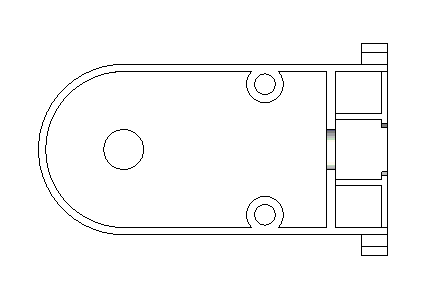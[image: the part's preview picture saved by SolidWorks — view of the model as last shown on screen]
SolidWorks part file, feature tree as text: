
SOLIDWORKS PART (.sldprt)
format: sldprt  version: not decoded by parser v0  size: 378,368 bytes
history: native  units: mm
features: sketch x12, cut_extrude x9, extrude x3, plane x1, mirror x1 (+10 scaffold rows collapsed)
feature tree (36):
  scaffold x10  (default folders/planes/origin — collapsed)
  sketch  "Sketch1"  dims[c1.D1=19.9644mm c1.D4=19.9644mm c2.D1=2.286mm c2.D2=2.9718mm c2.D3=2.413mm c2.D4=40.767mm c2.D5=9.9822mm]
  extrude  "Extrude1"  Depth=6.858mm
  sketch  "Sketch2"  dims[c1.D1=~1.497873mm c1.D3=3.0226mm c1.D4=3.0226mm c1.D5=3.0226mm c1.D6=7.2898mm c1.D7=2.032mm c1.D8=3.0226mm c2.D7=5.1562mm c2.D2=3.0226mm c2.D1=21.844mm c3.D2=13.6652mm c3.D3=8.382mm c3.D8=17.1196mm c3.D9=40.767mm c3.D7=30.7848mm c4.D2=8.382mm]
  extrude  "Extrude3"  Depth=0.254mm
  sketch  "Sketch7"  dims[D1=4.699mm]
  cut_extrude  "Cut-Extrude1"  [1 undecoded]
  sketch  "Sketch8"  dims[D1=1.3716mm D2=3.048mm]
  cut_extrude  "Cut-Extrude2"  [1 undecoded]
  sketch  "Sketch10"  dims[c1.D1=4.826mm c1.D2=0.889mm c1.D3=9.9822mm c1.D4=4.826mm c2.D1=4.826mm c2.D2=0.889mm c2.D3=0.889mm]
  cut_extrude  "Cut-Extrude3"  Depth=6.0706mm
  sketch  "Sketch11"  dims[c1.D1=5.334mm c1.D2=0.635mm c1.D3=0.127mm c2.D2=0.635mm c2.D1=4.9276mm c2.D3=0.635mm c2.D4=0.635mm]
  cut_extrude  "Cut-Extrude4"  Depth=0.9144mm
  sketch  "Sketch12"  dims[D1=2.54mm D2=3.048mm]
  cut_extrude  "Cut-Extrude10"  [1 undecoded]
  sketch  "Sketch15"  dims[D1=1.016mm]
  cut_extrude  "Cut-Extrude15"  [1 undecoded]
  sketch  "Sketch16"  dims[D1=~2.79016mm]
  cut_extrude  "Cut-Extrude16"  [1 undecoded]
  sketch  "Sketch19"  dims[D3=4.318mm D1=14.3002mm D2=2.3368mm]
  extrude  "Extrude5"  [1 undecoded]
  sketch  "Sketch20"  dims[D1=2.413mm]
  cut_extrude  "Cut-Extrude18"  Depth=6.985mm
  sketch  "Sketch21"  dims[D1=3.81mm]
  cut_extrude  "Cut-Extrude19"  Depth=1.0668mm
  plane  "Plane1"
  mirror  "Mirror1"
decode coverage: 18 of 25 modeling features carry decoded parameters
note: ~ marks probable driven/reference dimensions
note: 6 parameter values undecoded
summary: no parameter record found for 6 features
note: suppression state not decoded; provenance and decode notes live in map.json
